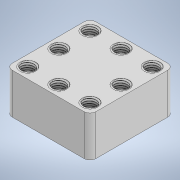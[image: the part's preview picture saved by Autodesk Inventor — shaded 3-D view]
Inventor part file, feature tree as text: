
AUTODESK INVENTOR PART (.ipt)
format: ipt  version: 2020 (Build 240168000, 168)  size: 7,534,080 bytes
history: native  units: mm
features: sketch x43, thread x17, revolve x17, helix x17, extrude x9, plane x2
ambient origin geometry x8: Origin, YZ Plane, XZ Plane, XY Plane, X Axis, Y Axis, Z Axis, Center Point
bodies: Solid1 (feature_tree), Solid19 (feature_tree), Solid20 (feature_tree), Solid21 (feature_tree), Solid22 (feature_tree), Solid23 (feature_tree), Solid24 (feature_tree), Solid25 (feature_tree), Solid26 (feature_tree), Solid27 (feature_tree), Solid28 (feature_tree), Solid29 (feature_tree), Solid30 (feature_tree), Solid31 (feature_tree), Solid32 (feature_tree), Solid33 (feature_tree), Solid34 (feature_tree), Solid35 (feature_tree)
feature tree (105):
  extrude  "Extrusion1"  Depth=13.157mm
  extrude  "Extrusion2"  Depth=26.0mm
  extrude  "Extrusion3"  Depth=10.0mm TaperAngle=0.0deg
  extrude  "Extrusion4"  Depth=26.0mm TaperAngle=0.0deg
  thread  "Thread25"  [1 undecoded]
  thread  "Thread26"  [1 undecoded]
  thread  "Thread27"  [1 undecoded]
  thread  "Thread28"  [1 undecoded]
  thread  "Thread29"  [1 undecoded]
  thread  "Thread30"  [1 undecoded]
  thread  "Thread31"  [1 undecoded]
  thread  "Thread32"  [1 undecoded]
  extrude  "Extrusion9"  Depth=19.0mm
  extrude  "Extrusion10"  Depth=5.0mm
  extrude  "Extrusion11"  TaperAngle=45.0deg  [1 undecoded]
  plane  "Work Plane2"
  extrude  "Extrusion12"  Depth=70.0mm TaperAngle=0.0deg
  extrude  "Extrusion14"  Depth=35.0mm TaperAngle=0.0deg
  thread  "Thread33"  [1 undecoded]
  thread  "Thread34"  [1 undecoded]
  thread  "Thread35"  [1 undecoded]
  thread  "Thread36"  [1 undecoded]
  thread  "Thread37"  [1 undecoded]
  thread  "Thread38"  [1 undecoded]
  thread  "Thread39"  [1 undecoded]
  thread  "Thread40"  [1 undecoded]
  thread  "Thread41"  [1 undecoded]
  revolve  "Revolution18"  [1 undecoded]
  helix  "Coil18"  [1 undecoded]
  revolve  "Revolution19"  [1 undecoded]
  helix  "Coil19"  [1 undecoded]
  revolve  "Revolution20"  [1 undecoded]
  helix  "Coil20"  [1 undecoded]
  revolve  "Revolution21"  [1 undecoded]
  helix  "Coil21"  [1 undecoded]
  revolve  "Revolution22"  [1 undecoded]
  helix  "Coil22"  [1 undecoded]
  revolve  "Revolution23"  [1 undecoded]
  helix  "Coil23"  [1 undecoded]
  revolve  "Revolution24"  [1 undecoded]
  helix  "Coil24"  [1 undecoded]
  revolve  "Revolution25"  [1 undecoded]
  helix  "Coil25"  [1 undecoded]
  revolve  "Revolution26"  [1 undecoded]
  helix  "Coil26"  [1 undecoded]
  revolve  "Revolution27"  [1 undecoded]
  helix  "Coil27"  [1 undecoded]
  revolve  "Revolution28"  [1 undecoded]
  helix  "Coil28"  [1 undecoded]
  revolve  "Revolution29"  [1 undecoded]
  helix  "Coil29"  [1 undecoded]
  revolve  "Revolution30"  [1 undecoded]
  helix  "Coil30"  [1 undecoded]
  revolve  "Revolution31"  [1 undecoded]
  helix  "Coil31"  [1 undecoded]
  revolve  "Revolution32"  [1 undecoded]
  helix  "Coil32"  [1 undecoded]
  revolve  "Revolution33"  [1 undecoded]
  helix  "Coil33"  [1 undecoded]
  revolve  "Revolution34"  [1 undecoded]
  helix  "Coil34"  [1 undecoded]
  sketch  "Sketch1"  dims[d0=70.0mm d1=70.0mm d2=5.0mm d3=34.0mm d4=0.0mm d5=13.157mm]
  sketch  "Sketch2"  dims[d7=26.0mm d8=26.0mm]
  sketch  "Sketch5"  dims[d9=30.0mm d11=26.0mm d12=30.0mm d14=26.0mm d17=10.0mm d18=0.0mm]
  sketch  "Sketch6"  dims[d20=30.0mm d22=30.0mm d23=9.0mm d24=26.0mm d25=26.0mm d26=26.0mm d27=26.0mm d28=12.0mm d29=0.0mm]
  sketch  "Sketch12"  dims[d31=30.0mm d33=30.0mm d34=7.25mm d35=26.0mm d36=26.0mm d37=26.0mm d38=26.0mm d39=13.5mm d40=0.0mm d107=7.0mm d108=0.0mm d109=7.0mm d110=0.0mm d111=7.0mm d112=0.0mm d113=7.0mm d114=0.0mm d115=7.0mm d116=0.0mm d117=7.0mm d118=0.0mm d119=7.0mm d120=0.0mm d121=7.0mm d122=0.0mm d123=10.9mm]
  sketch  "Sketch13"  dims[d124=19.0mm d125=0.0mm d126=5.0mm]
  sketch  "Sketch14"  dims[d127=50.0mm d128=0.0mm d129=5.0mm]
  plane  "Work Plane1"
  sketch  "Sketch15"  dims[d130=50.0mm d131=0.0mm d132=45.0deg d133=90.0deg]
  sketch  "Sketch17"  dims[d134=5.0mm d135=70.0mm d136=0.0mm]
  sketch  "Sketch52"  dims[d140=5.0mm d141=35.0mm d142=0.0mm d143=6.0mm d144=0.0mm d145=6.0mm d146=0.0mm d147=6.0mm d148=0.0mm d149=6.0mm d150=0.0mm d151=6.0mm d152=0.0mm d153=6.0mm d154=0.0mm d155=6.0mm d156=0.0mm d157=6.0mm d158=0.0mm d159=6.0mm d160=0.0mm]
  sketch  "Sketch53"  dims[d168=9.599311mm d186=9.599311mm d204=9.599311mm]
  sketch  "Sketch54"  dims[d222=9.599311mm d240=9.599311mm d258=9.599311mm]
  sketch  "Sketch55"  dims[d276=9.599311mm d294=9.599311mm d312=9.599311mm]
  sketch  "Sketch56"  dims[d330=9.599311mm d348=9.599311mm d366=9.599311mm]
  sketch  "Sketch57"  dims[d384=9.599311mm d402=9.599311mm d420=9.599311mm]
  sketch  "Sketch58"  dims[d438=9.599311mm d456=9.599311mm d467=9.599311mm d468=0.145218mm d469=0.145218mm]
  sketch  "Sketch59"  dims[d472=0.907143mm d474=9.599311mm d476=0.0mm]
  sketch  "Sketch60"  dims[d477=0.90805mm d478=7.814286mm d479=10.0mm d480=0.0mm d481=0.0mm d482=0.0mm d483=0.0mm d484=0.0mm d485=9.599311mm d486=0.145218mm d487=0.145218mm d490=0.907143mm]
  sketch  "Sketch61"  dims[d492=9.599311mm d494=0.0mm]
  sketch  "Sketch62"  dims[d495=0.90805mm d496=7.814286mm d497=10.0mm d498=0.0mm d499=0.0mm d500=0.0mm d501=0.0mm d502=0.0mm d503=9.599311mm d504=0.145218mm d505=0.145218mm]
  sketch  "Sketch63"  dims[d508=0.907143mm d510=9.599311mm d512=0.0mm]
  sketch  "Sketch64"  dims[d513=0.90805mm d514=7.814286mm d515=10.0mm d516=0.0mm d517=0.0mm d518=0.0mm d519=0.0mm d520=0.0mm d521=9.599311mm d522=0.145218mm d523=0.145218mm d526=0.907143mm]
  sketch  "Sketch65"  dims[d528=9.599311mm d530=0.0mm]
  sketch  "Sketch66"  dims[d531=0.90805mm d532=7.814286mm d533=10.0mm d534=0.0mm d535=0.0mm d536=0.0mm d537=0.0mm d538=0.0mm d539=9.599311mm d540=0.145218mm d541=0.145218mm]
  sketch  "Sketch67"  dims[d544=0.907143mm d546=9.599311mm d548=0.0mm]
  sketch  "Sketch68"  dims[d549=0.90805mm d550=7.814286mm d551=10.0mm d552=0.0mm d553=0.0mm d554=0.0mm d555=0.0mm d556=0.0mm d557=9.599311mm d558=0.145218mm d559=0.145218mm d562=0.907143mm]
  sketch  "Sketch69"  dims[d564=9.599311mm d566=0.0mm]
  sketch  "Sketch70"  dims[d567=0.90805mm d568=7.814286mm d569=10.0mm d570=0.0mm d571=0.0mm d572=0.0mm d573=0.0mm d574=0.0mm d575=9.599311mm d576=0.145218mm d577=0.145218mm]
  sketch  "Sketch71"  dims[d580=0.907143mm d582=9.599311mm d584=0.0mm]
  sketch  "Sketch72"  dims[d585=0.90805mm d586=7.814286mm d587=10.0mm d588=0.0mm d589=0.0mm d590=0.0mm d591=0.0mm d592=0.0mm d593=9.599311mm d594=0.145218mm d595=0.145218mm d598=0.907143mm]
  sketch  "Sketch73"  dims[d600=9.599311mm]
  sketch  "Sketch74"  dims[d602=0.0mm]
  sketch  "Sketch75"  dims[d603=0.90805mm d604=7.814286mm d605=10.0mm d606=0.0mm d607=0.0mm d608=0.0mm d609=0.0mm d610=0.0mm]
  sketch  "Sketch76"  dims[d611=9.599311mm d612=0.145218mm d613=0.145218mm]
  sketch  "Sketch77"  dims[d616=0.907143mm]
  sketch  "Sketch78"  dims[d618=9.599311mm]
  sketch  "Sketch79"  dims[d620=0.0mm]
  sketch  "Sketch80"  dims[d621=0.90805mm d622=7.814286mm d623=10.0mm d624=0.0mm d625=0.0mm d626=0.0mm d627=0.0mm d628=0.0mm]
  sketch  "Sketch81"  dims[d629=9.599311mm d630=0.290436mm d631=0.290436mm]
  sketch  "Sketch82"  dims[d634=1.814286mm]
  sketch  "Sketch83"  dims[d636=9.599311mm]
  sketch  "Sketch84"  dims[d638=0.0mm]
  sketch  "Sketch85"  dims[d639=1.8161mm d640=10.628571mm d641=10.0mm d642=0.0mm d643=0.0mm d644=0.0mm d645=0.0mm d646=0.0mm d647=9.599311mm d648=0.290436mm d649=0.290436mm d652=1.814286mm d654=9.599311mm d656=0.0mm d657=1.8161mm d658=10.628571mm d659=10.0mm d660=0.0mm d661=0.0mm d662=0.0mm d663=0.0mm d664=0.0mm d665=9.599311mm d666=0.290436mm d667=0.290436mm d670=1.814286mm d672=9.599311mm d674=0.0mm d675=1.8161mm d676=10.628571mm d677=10.0mm d678=0.0mm d679=0.0mm d680=0.0mm d681=0.0mm d682=0.0mm d683=9.599311mm d684=0.290436mm d685=0.290436mm d688=1.814286mm d690=9.599311mm d692=0.0mm d693=1.8161mm d694=10.628571mm d695=10.0mm d696=0.0mm d697=0.0mm d698=0.0mm d699=0.0mm d700=0.0mm d701=9.599311mm d702=0.290436mm d703=0.290436mm d706=1.814286mm d708=9.599311mm d710=0.0mm d711=1.8161mm d712=10.628571mm d713=10.0mm d714=0.0mm d715=0.0mm d716=0.0mm d717=0.0mm d718=0.0mm d719=9.599311mm d720=0.290436mm d721=0.290436mm d724=1.814286mm d726=9.599311mm d728=0.0mm d729=1.8161mm d730=10.628571mm d731=10.0mm d732=0.0mm d733=0.0mm d734=0.0mm d735=0.0mm d736=0.0mm d737=9.599311mm d738=0.290436mm d739=0.290436mm d742=1.814286mm d744=9.599311mm d746=0.0mm d747=1.8161mm d748=10.628571mm d749=10.0mm d750=0.0mm d751=0.0mm d752=0.0mm d753=0.0mm d754=0.0mm d755=9.599311mm d756=0.290436mm d757=0.290436mm d760=1.814286mm d762=9.599311mm d764=0.0mm d765=1.8161mm d766=10.628571mm d767=10.0mm d768=0.0mm d769=0.0mm d770=0.0mm d771=0.0mm d772=0.0mm]
note: 52 required parameter values undecoded (feature->parameter linkage not recoverable at this tier; creation-order binding heuristic only, values carry confidence <= 0.55)